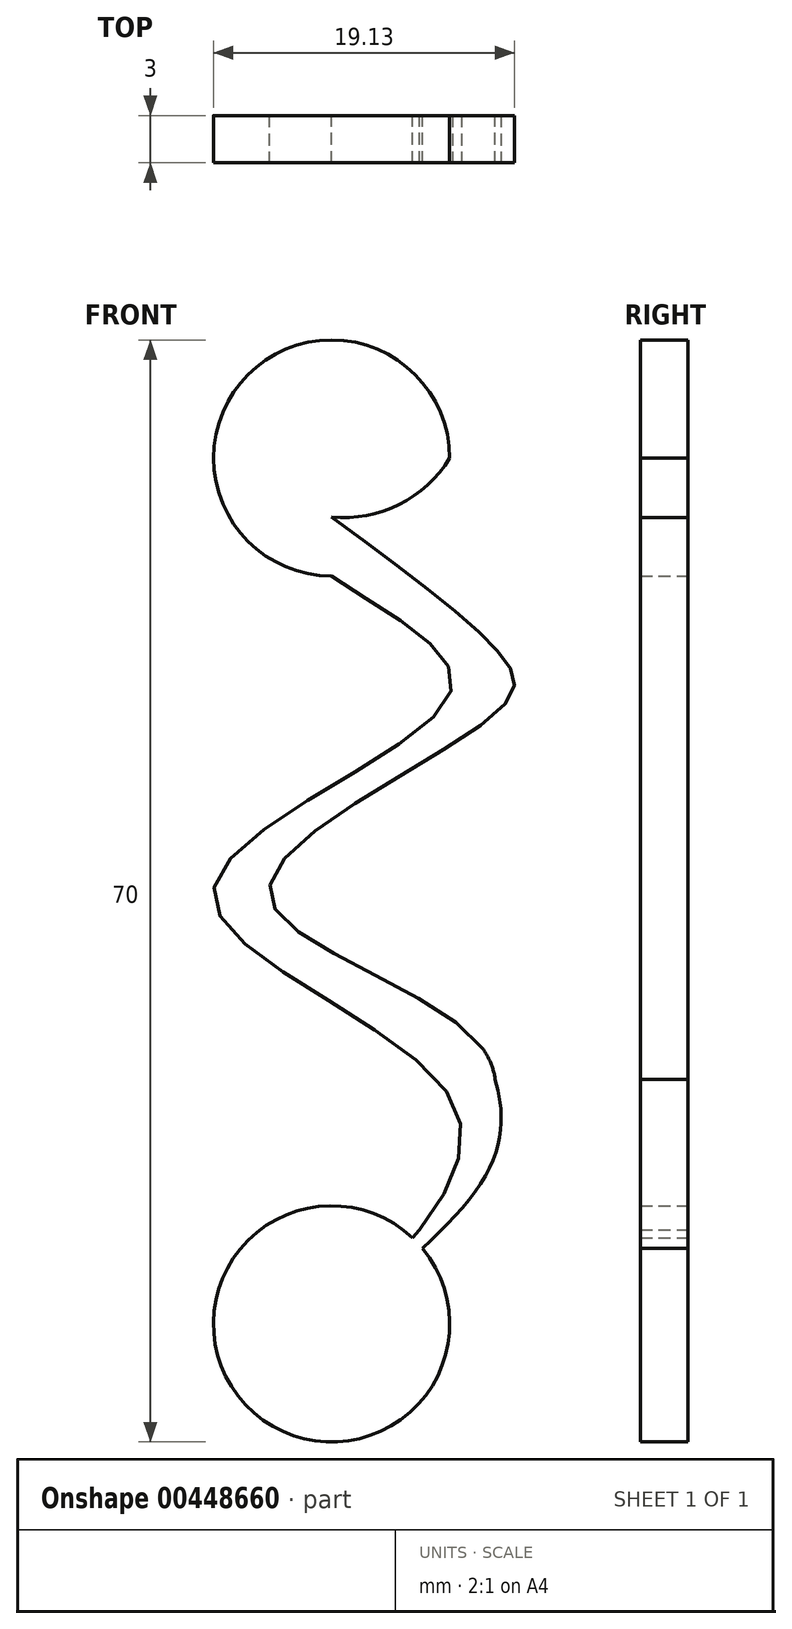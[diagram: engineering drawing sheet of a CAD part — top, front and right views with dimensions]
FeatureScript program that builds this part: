
annotation { "Feature Type Name" : "Feature", "Feature Type Description" : "" }
export const myFeature = defineFeature(function(context is Context, id is Id, definition is map)
    precondition{}
    {
        {
            var Q0;
            Q0=qCreatedBy(makeId("Front.planeOp"),FACE);
            var sketch = newSketch(context, id + "F0", { "sketchPlane" : qUnion([Q0])});
            skCircle(sketch, "E0", {"center": v(0, 0) * mm, "radius": 7.5 * mm});
            skLineSegment(sketch, "E1", {"start": v(0, 0) * mm, "end": v(0, 7.5) * mm, "construction": true});
            skArc(sketch, "E2", {"start": v(7.5, 55) * mm, "mid": v(-5.3, 60.3) * mm, "end": v(0, 47.5) * mm});
            skLineSegment(sketch, "E3", {"start": v(-7.5, 27.08) * mm, "end": v(-7.5, 27.5) * mm, "construction": true});
            skLineSegment(sketch, "E4", {"start": v(7.5, 0) * mm, "end": v(7.5, 14.45) * mm, "construction": true});
            skFitSpline(sketch, "E5", {"points": [v(0, 0) * mm, v(7.5, 14.45) * mm, v(-7.5, 27.5) * mm, v(7.5, 39.94) * mm, v(0, 47.5) * mm, v(-7.5, 55) * mm], "startDerivative": vector(73.53, 72.87) * mm, "endDerivative": vector(-35.45, 45.29) * mm});
            skCircle(sketch, "E6", {"center": v(0, 55) * mm, "radius": 3.75 * mm});
            skArc(sketch, "E7", {"start": v(0, 51.25) * mm, "mid": v(4.3, 52.04) * mm, "end": v(7.5, 55) * mm});
            skLineSegment(sketch, "E8", {"start": v(0, 51.25) * mm, "end": v(0, 47.5) * mm});
            skPoint(sketch, "E9.orphan", {"position": v(-7.5, 0) * mm});
            skLineSegment(sketch, "E10.trimOffspring", {"start": v(0, 47.5) * mm, "end": v(0, 55) * mm, "construction": true});
            skLineSegment(sketch, "E11.trimOffspring", {"start": v(7.5, 39.94) * mm, "end": v(7.5, 41.56) * mm, "construction": true});
            skFitSpline(sketch, "E12", {"points": [v(0, 51.25) * mm, v(10.62, 42.65) * mm, v(10.9, 39.25) * mm, v(-3.97, 27.5) * mm, v(9.63, 17.44) * mm, v(1.92, 1.92) * mm], "startDerivative": vector(63.24, -46.35) * mm, "endDerivative": vector(-69.2, -74.8) * mm});
            skFitSpline(sketch, "E13", {"points": [v(9.63, 17.44) * mm, v(10.4, 15.52) * mm, v(10.27, 10.43) * mm, v(0, 0) * mm], "startDerivative": vector(4.17, -8.75) * mm, "endDerivative": vector(-26.32, -20.98) * mm});
            skSolve(sketch);
        }
        {
            var Q0;
            Q0 = qSketchRegion(id + "F0", true);
            extrude(context, id + "F1", {"entities" : qUnion([Q0]), "depth" : 3 * mm});
        }
    });
